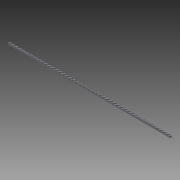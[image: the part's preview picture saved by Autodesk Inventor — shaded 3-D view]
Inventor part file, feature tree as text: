
AUTODESK INVENTOR PART (.ipt)
format: ipt  version: 2013 (Build 170138000, 138)  size: 2,534,912 bytes
history: native  units: in
note: dims shown in document units (in); Inventor stores cm internally (conversion verified against a paired STEP export)
features: extrude x2, sketch x2, pattern_linear x1
ambient origin geometry x8: Origin, YZ Plane, XZ Plane, XY Plane, X Axis, Y Axis, Z Axis, Center Point
bodies: Solid1 (feature_tree)
feature tree (5):
  extrude  "Extrusion1"  Depth=0.5in
  extrude  "Extrusion2"  Depth=0.05in
  pattern_linear  "Rectangular Pattern2"  Spacing1=0.7559in  [1 undecoded]
  sketch  "Sketch1"  dims[d0=0.5in d1=0.5in]
  sketch  "Sketch2"  dims[d3=0.0in d8=0.05in d9=0.7559in d10=0.7559in d11=72.0in d12=0.0in d17=0.0167in d18=0.0333in d19=0.035in d20=566.9291in d22=0.05in]
note: 1 required parameter value undecoded (feature->parameter linkage not recoverable at this tier; creation-order binding heuristic only, values carry confidence <= 0.55)
